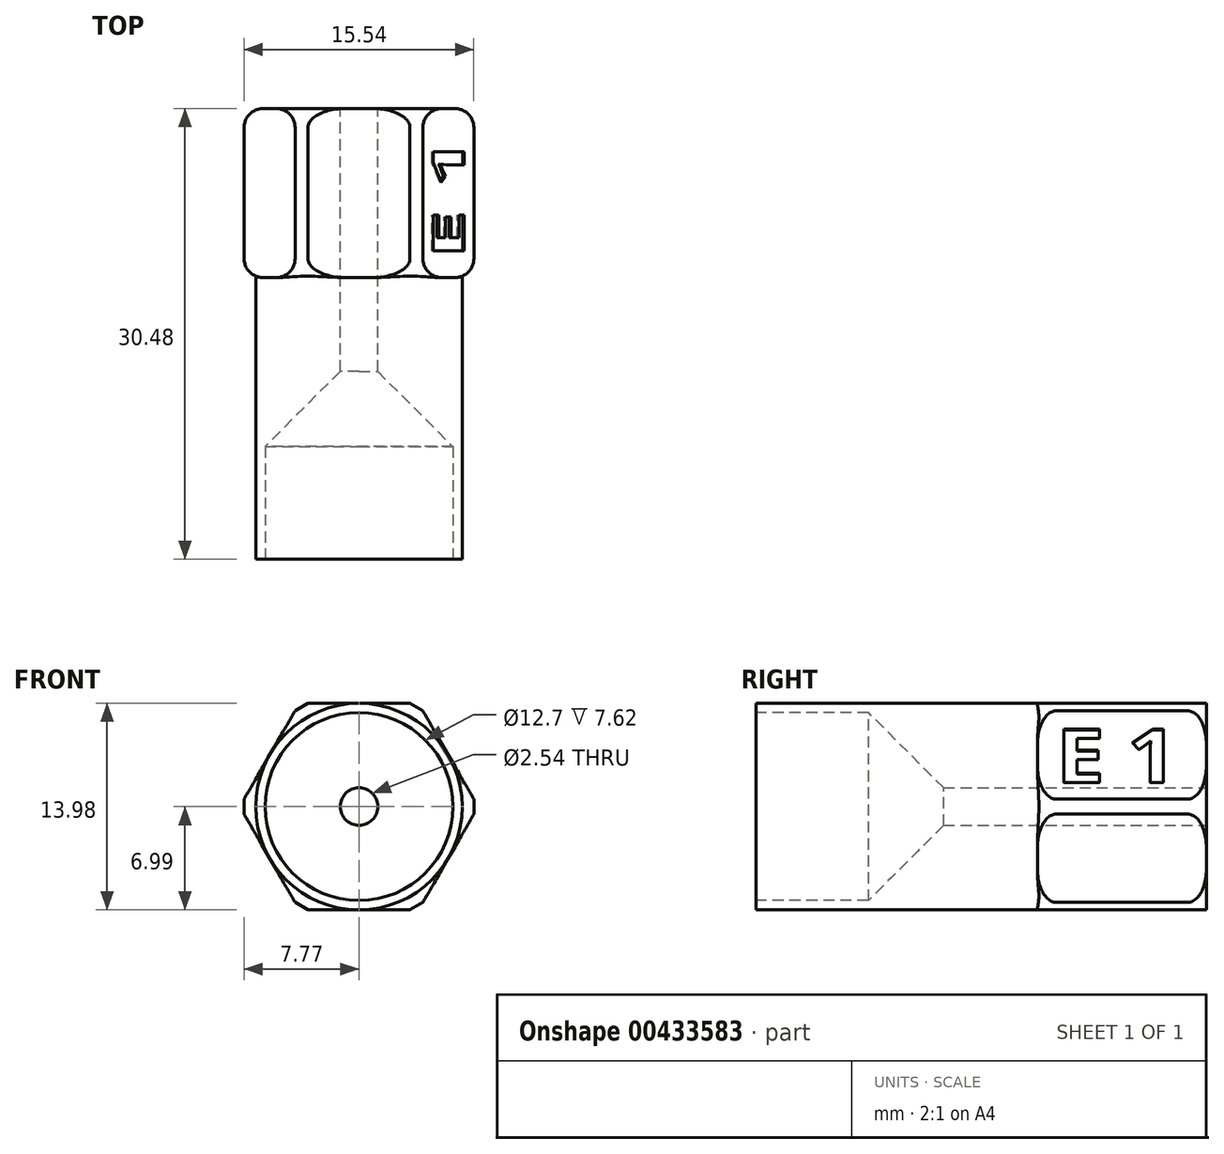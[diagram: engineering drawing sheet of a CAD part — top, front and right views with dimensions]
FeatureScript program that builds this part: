
annotation { "Feature Type Name" : "Feature", "Feature Type Description" : "" }
export const myFeature = defineFeature(function(context is Context, id is Id, definition is map)
    precondition{}
    {
        {
            var Q0;
            Q0=qCreatedBy(makeId("Front.planeOp"),FACE);
            var sketch = newSketch(context, id + "F0", { "sketchPlane" : qUnion([Q0])});
            skCircle(sketch, "E0.cCircle", {"center": v(0, 0) * mm, "radius": 6.99 * mm, "construction": true});
            skLineSegment(sketch, "E0.0", {"start": v(-4.03, 6.99) * mm, "end": v(4.03, 6.99) * mm});
            skLineSegment(sketch, "E0.1", {"start": v(4.03, 6.99) * mm, "end": v(8.07, 0) * mm});
            skLineSegment(sketch, "E0.2", {"start": v(8.07, 0) * mm, "end": v(4.03, -6.98) * mm});
            skLineSegment(sketch, "E0.3", {"start": v(4.03, -6.98) * mm, "end": v(-4.03, -6.99) * mm});
            skLineSegment(sketch, "E0.4", {"start": v(-4.03, -6.99) * mm, "end": v(-8.07, 0) * mm});
            skLineSegment(sketch, "E0.5", {"start": v(-8.07, 0) * mm, "end": v(-4.03, 6.99) * mm});
            skPoint(sketch, "E0.0.midPoint", {"position": v(0, 6.99) * mm});
            skSolve(sketch);
        }
        {
            var Q0;
            Q0=makeQuery(id+"F0.imprint","IMPRINT",FACE,{"disambiguationData":[TD([[makeQuery(id+"F0.imprint","IMPRINT",EDGE,{"derivedFrom":sQuery(id+"F0.wireOp",EDGE,"E0.0")}),-1.0]])]});
            extrude(context, id + "F1", {"entities" : qUnion([Q0]), "depth" : 11.43 * mm});
        }
        {
            var Q0;
            Q0=makeQuery(id+"F1.opExtrude","CAP_FACE",FACE,{"disambiguationData":[OSD([sQuery(id+"F0.wireOp",EDGE,"E0.0"),sQuery(id+"F0.wireOp",EDGE,"E0.1"),sQuery(id+"F0.wireOp",EDGE,"E0.2"),sQuery(id+"F0.wireOp",EDGE,"E0.3"),sQuery(id+"F0.wireOp",EDGE,"E0.4"),sQuery(id+"F0.wireOp",EDGE,"E0.5")])],"isStart":false});
            var sketch = newSketch(context, id + "F2", { "sketchPlane" : qUnion([Q0])});
            skCircle(sketch, "E1", {"center": v(0, 0) * mm, "radius": 6.99 * mm});
            skSolve(sketch);
        }
        {
            var Q0;
            {var subQ0=sQuery(id+"F2.wireOp",EDGE,"E1");var subQ4=makeQuery(id+"F2.imprint","INTERSECT",VERTEX,{"derivedFrom":[makeQuery(id+"F1.opExtrude","CAP_EDGE",EDGE,{"disambiguationData":[OSD([sQuery(id+"F0.wireOp",EDGE,"E0.0")])],"isStart":false}),subQ0]});Q0=makeQuery(id+"F2.imprint","IMPRINT",FACE,{"disambiguationData":[TD([[makeQuery(id+"F2.imprint","IMPRINT",EDGE,{"disambiguationData":[TD([[subQ4,1.0]])],"derivedFrom":subQ0}),1.0]])]});}
            extrude(context, id + "F3", {"entities" : qUnion([Q0]), "operationType" : NewBodyOperationType.ADD, "depth" : 19.05 * mm});
        }
        {
            var Q0;
            Q0=makeQuery(id+"F3.opExtrude","CAP_FACE",FACE,{"disambiguationData":[OSD([sQuery(id+"F2.wireOp",EDGE,"E1")])],"isStart":false});
            var sketch = newSketch(context, id + "F4", { "sketchPlane" : qUnion([Q0])});
            skCircle(sketch, "E2", {"center": v(0, 0) * mm, "radius": 6.35 * mm});
            skSolve(sketch);
        }
        {
            var Q0;
            Q0=makeQuery(id+"F4.imprint","IMPRINT",FACE,{"disambiguationData":[TD([[makeQuery(id+"F4.imprint","IMPRINT",EDGE,{"derivedFrom":sQuery(id+"F4.wireOp",EDGE,"E2")}),1.0]])]});
            extrude(context, id + "F5", {"entities" : qUnion([Q0]), "operationType" : NewBodyOperationType.REMOVE, "oppositeDirection" : true, "depth" : 12.7 * mm});
        }
        {
            var Q0;
            Q0=makeQuery(id+"F5.boolean.opBoolean","COPY",EDGE,{"derivedFrom":makeQuery(id+"F5.opExtrude","CAP_EDGE",EDGE,{"disambiguationData":[OSD([sQuery(id+"F4.wireOp",EDGE,"E2")])],"isStart":false})});
            chamfer(context, id + "F6", {"entities" : qUnion([Q0]), "width" : 5.08 * mm, "tangentPropagation" : true});
        }
        {
            var Q0;
            Q0=makeQuery(id+"F1.opExtrude","SWEPT_EDGE",EDGE,{"disambiguationData":[OSD([sQuery(id+"F0.wireOp",EDGE,"E0.0"),sQuery(id+"F0.wireOp",EDGE,"E0.5")])]});
            var Q1;
            Q1=makeQuery(id+"F1.opExtrude","SWEPT_EDGE",EDGE,{"disambiguationData":[OSD([sQuery(id+"F0.wireOp",EDGE,"E0.0"),sQuery(id+"F0.wireOp",EDGE,"E0.1")])]});
            var Q2;
            Q2=makeQuery(id+"F1.opExtrude","SWEPT_EDGE",EDGE,{"disambiguationData":[OSD([sQuery(id+"F0.wireOp",EDGE,"E0.1"),sQuery(id+"F0.wireOp",EDGE,"E0.2")])]});
            var Q3;
            Q3=makeQuery(id+"F1.opExtrude","SWEPT_EDGE",EDGE,{"disambiguationData":[OSD([sQuery(id+"F0.wireOp",EDGE,"E0.2"),sQuery(id+"F0.wireOp",EDGE,"E0.3")])]});
            var Q4;
            Q4=makeQuery(id+"F1.opExtrude","SWEPT_EDGE",EDGE,{"disambiguationData":[OSD([sQuery(id+"F0.wireOp",EDGE,"E0.3"),sQuery(id+"F0.wireOp",EDGE,"E0.4")])]});
            var Q5;
            Q5=makeQuery(id+"F1.opExtrude","SWEPT_EDGE",EDGE,{"disambiguationData":[OSD([sQuery(id+"F0.wireOp",EDGE,"E0.4"),sQuery(id+"F0.wireOp",EDGE,"E0.5")])]});
            chamfer(context, id + "F7", {"entities" : qUnion([Q0, Q1, Q2, Q3, Q4, Q5]), "width" : 1.02 * mm, "tangentPropagation" : true});
        }
        {
            var Q0;
            {var subQ0=sQuery(id+"F0.wireOp",EDGE,"E0.2");var subQ1=sQuery(id+"F0.wireOp",EDGE,"E0.1");var subQ2=makeQuery(id+"F1.opExtrude","CAP_FACE",FACE,{"disambiguationData":[OSD([sQuery(id+"F0.wireOp",EDGE,"E0.0"),subQ1,subQ0,sQuery(id+"F0.wireOp",EDGE,"E0.3"),sQuery(id+"F0.wireOp",EDGE,"E0.4"),sQuery(id+"F0.wireOp",EDGE,"E0.5")])],"isStart":false});Q0=makeQuery(id+"F7.opChamfer","BLEND_EDGE",EDGE,{"blendedFrom":[makeQuery(id+"F1.opExtrude","SWEPT_EDGE",EDGE,{"disambiguationData":[OSD([subQ1,subQ0])]}),makeQuery(id+"F3.boolean.opBoolean","SPLIT",FACE,{"disambiguationData":[TD([subQ2,makeQuery(id+"F1.opExtrude","SWEPT_FACE",FACE,{"disambiguationData":[OSD([subQ1])]}),makeQuery(id+"F1.opExtrude","SWEPT_FACE",FACE,{"disambiguationData":[OSD([subQ0])]}),makeQuery(id+"F3.opExtrude","SWEPT_FACE",FACE,{"disambiguationData":[OSD([sQuery(id+"F2.wireOp",EDGE,"E1")])]})])],"derivedFrom":subQ2})],"blendedInto":[makeQuery(id+"F3.boolean.opBoolean","SPLIT",FACE,{"disambiguationData":[TD([subQ2,makeQuery(id+"F1.opExtrude","SWEPT_FACE",FACE,{"disambiguationData":[OSD([subQ1])]}),makeQuery(id+"F1.opExtrude","SWEPT_FACE",FACE,{"disambiguationData":[OSD([subQ0])]}),makeQuery(id+"F3.opExtrude","SWEPT_FACE",FACE,{"disambiguationData":[OSD([sQuery(id+"F2.wireOp",EDGE,"E1")])]})])],"derivedFrom":subQ2})]});}
            var Q1;
            {var subQ0=sQuery(id+"F0.wireOp",EDGE,"E0.3");var subQ1=sQuery(id+"F0.wireOp",EDGE,"E0.2");var subQ2=makeQuery(id+"F1.opExtrude","CAP_FACE",FACE,{"disambiguationData":[OSD([sQuery(id+"F0.wireOp",EDGE,"E0.0"),sQuery(id+"F0.wireOp",EDGE,"E0.1"),subQ1,subQ0,sQuery(id+"F0.wireOp",EDGE,"E0.4"),sQuery(id+"F0.wireOp",EDGE,"E0.5")])],"isStart":false});Q1=makeQuery(id+"F7.opChamfer","BLEND_EDGE",EDGE,{"blendedFrom":[makeQuery(id+"F1.opExtrude","SWEPT_EDGE",EDGE,{"disambiguationData":[OSD([subQ1,subQ0])]}),makeQuery(id+"F3.boolean.opBoolean","SPLIT",FACE,{"disambiguationData":[TD([subQ2,makeQuery(id+"F1.opExtrude","SWEPT_FACE",FACE,{"disambiguationData":[OSD([subQ1])]}),makeQuery(id+"F1.opExtrude","SWEPT_FACE",FACE,{"disambiguationData":[OSD([subQ0])]}),makeQuery(id+"F3.opExtrude","SWEPT_FACE",FACE,{"disambiguationData":[OSD([sQuery(id+"F2.wireOp",EDGE,"E1")])]})])],"derivedFrom":subQ2})],"blendedInto":[makeQuery(id+"F3.boolean.opBoolean","SPLIT",FACE,{"disambiguationData":[TD([subQ2,makeQuery(id+"F1.opExtrude","SWEPT_FACE",FACE,{"disambiguationData":[OSD([subQ1])]}),makeQuery(id+"F1.opExtrude","SWEPT_FACE",FACE,{"disambiguationData":[OSD([subQ0])]}),makeQuery(id+"F3.opExtrude","SWEPT_FACE",FACE,{"disambiguationData":[OSD([sQuery(id+"F2.wireOp",EDGE,"E1")])]})])],"derivedFrom":subQ2})]});}
            var Q2;
            {var subQ0=sQuery(id+"F0.wireOp",EDGE,"E0.4");var subQ1=sQuery(id+"F0.wireOp",EDGE,"E0.3");var subQ2=makeQuery(id+"F1.opExtrude","CAP_FACE",FACE,{"disambiguationData":[OSD([sQuery(id+"F0.wireOp",EDGE,"E0.0"),sQuery(id+"F0.wireOp",EDGE,"E0.1"),sQuery(id+"F0.wireOp",EDGE,"E0.2"),subQ1,subQ0,sQuery(id+"F0.wireOp",EDGE,"E0.5")])],"isStart":false});Q2=makeQuery(id+"F7.opChamfer","BLEND_EDGE",EDGE,{"blendedFrom":[makeQuery(id+"F1.opExtrude","SWEPT_EDGE",EDGE,{"disambiguationData":[OSD([subQ1,subQ0])]}),makeQuery(id+"F3.boolean.opBoolean","SPLIT",FACE,{"disambiguationData":[TD([subQ2,makeQuery(id+"F1.opExtrude","SWEPT_FACE",FACE,{"disambiguationData":[OSD([subQ1])]}),makeQuery(id+"F1.opExtrude","SWEPT_FACE",FACE,{"disambiguationData":[OSD([subQ0])]}),makeQuery(id+"F3.opExtrude","SWEPT_FACE",FACE,{"disambiguationData":[OSD([sQuery(id+"F2.wireOp",EDGE,"E1")])]})])],"derivedFrom":subQ2})],"blendedInto":[makeQuery(id+"F3.boolean.opBoolean","SPLIT",FACE,{"disambiguationData":[TD([subQ2,makeQuery(id+"F1.opExtrude","SWEPT_FACE",FACE,{"disambiguationData":[OSD([subQ1])]}),makeQuery(id+"F1.opExtrude","SWEPT_FACE",FACE,{"disambiguationData":[OSD([subQ0])]}),makeQuery(id+"F3.opExtrude","SWEPT_FACE",FACE,{"disambiguationData":[OSD([sQuery(id+"F2.wireOp",EDGE,"E1")])]})])],"derivedFrom":subQ2})]});}
            var Q3;
            {var subQ0=sQuery(id+"F0.wireOp",EDGE,"E0.5");var subQ1=sQuery(id+"F0.wireOp",EDGE,"E0.4");var subQ2=makeQuery(id+"F1.opExtrude","CAP_FACE",FACE,{"disambiguationData":[OSD([sQuery(id+"F0.wireOp",EDGE,"E0.0"),sQuery(id+"F0.wireOp",EDGE,"E0.1"),sQuery(id+"F0.wireOp",EDGE,"E0.2"),sQuery(id+"F0.wireOp",EDGE,"E0.3"),subQ1,subQ0])],"isStart":false});Q3=makeQuery(id+"F7.opChamfer","BLEND_EDGE",EDGE,{"blendedFrom":[makeQuery(id+"F1.opExtrude","SWEPT_EDGE",EDGE,{"disambiguationData":[OSD([subQ1,subQ0])]}),makeQuery(id+"F3.boolean.opBoolean","SPLIT",FACE,{"disambiguationData":[TD([subQ2,makeQuery(id+"F1.opExtrude","SWEPT_FACE",FACE,{"disambiguationData":[OSD([subQ1])]}),makeQuery(id+"F1.opExtrude","SWEPT_FACE",FACE,{"disambiguationData":[OSD([subQ0])]}),makeQuery(id+"F3.opExtrude","SWEPT_FACE",FACE,{"disambiguationData":[OSD([sQuery(id+"F2.wireOp",EDGE,"E1")])]})])],"derivedFrom":subQ2})],"blendedInto":[makeQuery(id+"F3.boolean.opBoolean","SPLIT",FACE,{"disambiguationData":[TD([subQ2,makeQuery(id+"F1.opExtrude","SWEPT_FACE",FACE,{"disambiguationData":[OSD([subQ1])]}),makeQuery(id+"F1.opExtrude","SWEPT_FACE",FACE,{"disambiguationData":[OSD([subQ0])]}),makeQuery(id+"F3.opExtrude","SWEPT_FACE",FACE,{"disambiguationData":[OSD([sQuery(id+"F2.wireOp",EDGE,"E1")])]})])],"derivedFrom":subQ2})]});}
            var Q4;
            {var subQ0=sQuery(id+"F0.wireOp",EDGE,"E0.0");var subQ1=sQuery(id+"F0.wireOp",EDGE,"E0.5");var subQ2=makeQuery(id+"F1.opExtrude","CAP_FACE",FACE,{"disambiguationData":[OSD([subQ0,sQuery(id+"F0.wireOp",EDGE,"E0.1"),sQuery(id+"F0.wireOp",EDGE,"E0.2"),sQuery(id+"F0.wireOp",EDGE,"E0.3"),sQuery(id+"F0.wireOp",EDGE,"E0.4"),subQ1])],"isStart":false});Q4=makeQuery(id+"F7.opChamfer","BLEND_EDGE",EDGE,{"blendedFrom":[makeQuery(id+"F1.opExtrude","SWEPT_EDGE",EDGE,{"disambiguationData":[OSD([subQ0,subQ1])]}),makeQuery(id+"F3.boolean.opBoolean","SPLIT",FACE,{"disambiguationData":[TD([makeQuery(id+"F1.opExtrude","SWEPT_FACE",FACE,{"disambiguationData":[OSD([subQ0])]}),subQ2,makeQuery(id+"F1.opExtrude","SWEPT_FACE",FACE,{"disambiguationData":[OSD([subQ1])]}),makeQuery(id+"F3.opExtrude","SWEPT_FACE",FACE,{"disambiguationData":[OSD([sQuery(id+"F2.wireOp",EDGE,"E1")])]})])],"derivedFrom":subQ2})],"blendedInto":[makeQuery(id+"F3.boolean.opBoolean","SPLIT",FACE,{"disambiguationData":[TD([makeQuery(id+"F1.opExtrude","SWEPT_FACE",FACE,{"disambiguationData":[OSD([subQ0])]}),subQ2,makeQuery(id+"F1.opExtrude","SWEPT_FACE",FACE,{"disambiguationData":[OSD([subQ1])]}),makeQuery(id+"F3.opExtrude","SWEPT_FACE",FACE,{"disambiguationData":[OSD([sQuery(id+"F2.wireOp",EDGE,"E1")])]})])],"derivedFrom":subQ2})]});}
            var Q5;
            {var subQ0=sQuery(id+"F0.wireOp",EDGE,"E0.0");var subQ1=sQuery(id+"F0.wireOp",EDGE,"E0.1");var subQ2=makeQuery(id+"F1.opExtrude","CAP_FACE",FACE,{"disambiguationData":[OSD([subQ0,subQ1,sQuery(id+"F0.wireOp",EDGE,"E0.2"),sQuery(id+"F0.wireOp",EDGE,"E0.3"),sQuery(id+"F0.wireOp",EDGE,"E0.4"),sQuery(id+"F0.wireOp",EDGE,"E0.5")])],"isStart":false});Q5=makeQuery(id+"F7.opChamfer","BLEND_EDGE",EDGE,{"blendedFrom":[makeQuery(id+"F1.opExtrude","SWEPT_EDGE",EDGE,{"disambiguationData":[OSD([subQ0,subQ1])]}),makeQuery(id+"F3.boolean.opBoolean","SPLIT",FACE,{"disambiguationData":[TD([makeQuery(id+"F1.opExtrude","SWEPT_FACE",FACE,{"disambiguationData":[OSD([subQ0])]}),subQ2,makeQuery(id+"F1.opExtrude","SWEPT_FACE",FACE,{"disambiguationData":[OSD([subQ1])]}),makeQuery(id+"F3.opExtrude","SWEPT_FACE",FACE,{"disambiguationData":[OSD([sQuery(id+"F2.wireOp",EDGE,"E1")])]})])],"derivedFrom":subQ2})],"blendedInto":[makeQuery(id+"F3.boolean.opBoolean","SPLIT",FACE,{"disambiguationData":[TD([makeQuery(id+"F1.opExtrude","SWEPT_FACE",FACE,{"disambiguationData":[OSD([subQ0])]}),subQ2,makeQuery(id+"F1.opExtrude","SWEPT_FACE",FACE,{"disambiguationData":[OSD([subQ1])]}),makeQuery(id+"F3.opExtrude","SWEPT_FACE",FACE,{"disambiguationData":[OSD([sQuery(id+"F2.wireOp",EDGE,"E1")])]})])],"derivedFrom":subQ2})]});}
            var Q6;
            {var subQ0=sQuery(id+"F0.wireOp",EDGE,"E0.2");var subQ1=sQuery(id+"F0.wireOp",EDGE,"E0.1");Q6=makeQuery(id+"F7.opChamfer","BLEND_EDGE",EDGE,{"blendedFrom":[makeQuery(id+"F1.opExtrude","SWEPT_EDGE",EDGE,{"disambiguationData":[OSD([subQ1,subQ0])]}),makeQuery(id+"F1.opExtrude","CAP_FACE",FACE,{"disambiguationData":[OSD([sQuery(id+"F0.wireOp",EDGE,"E0.0"),subQ1,subQ0,sQuery(id+"F0.wireOp",EDGE,"E0.3"),sQuery(id+"F0.wireOp",EDGE,"E0.4"),sQuery(id+"F0.wireOp",EDGE,"E0.5")])],"isStart":true})],"blendedInto":[makeQuery(id+"F1.opExtrude","CAP_FACE",FACE,{"disambiguationData":[OSD([sQuery(id+"F0.wireOp",EDGE,"E0.0"),subQ1,subQ0,sQuery(id+"F0.wireOp",EDGE,"E0.3"),sQuery(id+"F0.wireOp",EDGE,"E0.4"),sQuery(id+"F0.wireOp",EDGE,"E0.5")])],"isStart":true})]});}
            var Q7;
            {var subQ0=sQuery(id+"F0.wireOp",EDGE,"E0.3");var subQ1=sQuery(id+"F0.wireOp",EDGE,"E0.2");Q7=makeQuery(id+"F7.opChamfer","BLEND_EDGE",EDGE,{"blendedFrom":[makeQuery(id+"F1.opExtrude","SWEPT_EDGE",EDGE,{"disambiguationData":[OSD([subQ1,subQ0])]}),makeQuery(id+"F1.opExtrude","CAP_FACE",FACE,{"disambiguationData":[OSD([sQuery(id+"F0.wireOp",EDGE,"E0.0"),sQuery(id+"F0.wireOp",EDGE,"E0.1"),subQ1,subQ0,sQuery(id+"F0.wireOp",EDGE,"E0.4"),sQuery(id+"F0.wireOp",EDGE,"E0.5")])],"isStart":true})],"blendedInto":[makeQuery(id+"F1.opExtrude","CAP_FACE",FACE,{"disambiguationData":[OSD([sQuery(id+"F0.wireOp",EDGE,"E0.0"),sQuery(id+"F0.wireOp",EDGE,"E0.1"),subQ1,subQ0,sQuery(id+"F0.wireOp",EDGE,"E0.4"),sQuery(id+"F0.wireOp",EDGE,"E0.5")])],"isStart":true})]});}
            var Q8;
            {var subQ0=sQuery(id+"F0.wireOp",EDGE,"E0.4");var subQ1=sQuery(id+"F0.wireOp",EDGE,"E0.3");Q8=makeQuery(id+"F7.opChamfer","BLEND_EDGE",EDGE,{"blendedFrom":[makeQuery(id+"F1.opExtrude","SWEPT_EDGE",EDGE,{"disambiguationData":[OSD([subQ1,subQ0])]}),makeQuery(id+"F1.opExtrude","CAP_FACE",FACE,{"disambiguationData":[OSD([sQuery(id+"F0.wireOp",EDGE,"E0.0"),sQuery(id+"F0.wireOp",EDGE,"E0.1"),sQuery(id+"F0.wireOp",EDGE,"E0.2"),subQ1,subQ0,sQuery(id+"F0.wireOp",EDGE,"E0.5")])],"isStart":true})],"blendedInto":[makeQuery(id+"F1.opExtrude","CAP_FACE",FACE,{"disambiguationData":[OSD([sQuery(id+"F0.wireOp",EDGE,"E0.0"),sQuery(id+"F0.wireOp",EDGE,"E0.1"),sQuery(id+"F0.wireOp",EDGE,"E0.2"),subQ1,subQ0,sQuery(id+"F0.wireOp",EDGE,"E0.5")])],"isStart":true})]});}
            var Q9;
            {var subQ0=sQuery(id+"F0.wireOp",EDGE,"E0.5");var subQ1=sQuery(id+"F0.wireOp",EDGE,"E0.4");Q9=makeQuery(id+"F7.opChamfer","BLEND_EDGE",EDGE,{"blendedFrom":[makeQuery(id+"F1.opExtrude","SWEPT_EDGE",EDGE,{"disambiguationData":[OSD([subQ1,subQ0])]}),makeQuery(id+"F1.opExtrude","CAP_FACE",FACE,{"disambiguationData":[OSD([sQuery(id+"F0.wireOp",EDGE,"E0.0"),sQuery(id+"F0.wireOp",EDGE,"E0.1"),sQuery(id+"F0.wireOp",EDGE,"E0.2"),sQuery(id+"F0.wireOp",EDGE,"E0.3"),subQ1,subQ0])],"isStart":true})],"blendedInto":[makeQuery(id+"F1.opExtrude","CAP_FACE",FACE,{"disambiguationData":[OSD([sQuery(id+"F0.wireOp",EDGE,"E0.0"),sQuery(id+"F0.wireOp",EDGE,"E0.1"),sQuery(id+"F0.wireOp",EDGE,"E0.2"),sQuery(id+"F0.wireOp",EDGE,"E0.3"),subQ1,subQ0])],"isStart":true})]});}
            var Q10;
            {var subQ0=sQuery(id+"F0.wireOp",EDGE,"E0.5");var subQ1=sQuery(id+"F0.wireOp",EDGE,"E0.0");Q10=makeQuery(id+"F7.opChamfer","BLEND_EDGE",EDGE,{"blendedFrom":[makeQuery(id+"F1.opExtrude","SWEPT_EDGE",EDGE,{"disambiguationData":[OSD([subQ1,subQ0])]}),makeQuery(id+"F1.opExtrude","CAP_FACE",FACE,{"disambiguationData":[OSD([subQ1,sQuery(id+"F0.wireOp",EDGE,"E0.1"),sQuery(id+"F0.wireOp",EDGE,"E0.2"),sQuery(id+"F0.wireOp",EDGE,"E0.3"),sQuery(id+"F0.wireOp",EDGE,"E0.4"),subQ0])],"isStart":true})],"blendedInto":[makeQuery(id+"F1.opExtrude","CAP_FACE",FACE,{"disambiguationData":[OSD([subQ1,sQuery(id+"F0.wireOp",EDGE,"E0.1"),sQuery(id+"F0.wireOp",EDGE,"E0.2"),sQuery(id+"F0.wireOp",EDGE,"E0.3"),sQuery(id+"F0.wireOp",EDGE,"E0.4"),subQ0])],"isStart":true})]});}
            var Q11;
            {var subQ0=sQuery(id+"F0.wireOp",EDGE,"E0.1");var subQ1=sQuery(id+"F0.wireOp",EDGE,"E0.0");Q11=makeQuery(id+"F7.opChamfer","BLEND_EDGE",EDGE,{"blendedFrom":[makeQuery(id+"F1.opExtrude","SWEPT_EDGE",EDGE,{"disambiguationData":[OSD([subQ1,subQ0])]}),makeQuery(id+"F1.opExtrude","CAP_FACE",FACE,{"disambiguationData":[OSD([subQ1,subQ0,sQuery(id+"F0.wireOp",EDGE,"E0.2"),sQuery(id+"F0.wireOp",EDGE,"E0.3"),sQuery(id+"F0.wireOp",EDGE,"E0.4"),sQuery(id+"F0.wireOp",EDGE,"E0.5")])],"isStart":true})],"blendedInto":[makeQuery(id+"F1.opExtrude","CAP_FACE",FACE,{"disambiguationData":[OSD([subQ1,subQ0,sQuery(id+"F0.wireOp",EDGE,"E0.2"),sQuery(id+"F0.wireOp",EDGE,"E0.3"),sQuery(id+"F0.wireOp",EDGE,"E0.4"),sQuery(id+"F0.wireOp",EDGE,"E0.5")])],"isStart":true})]});}
            fillet(context, id + "F8", {"entities" : qUnion([Q0, Q1, Q2, Q3, Q4, Q5, Q6, Q7, Q8, Q9, Q10, Q11]), "radius" : 1.27 * mm, "tangentPropagation" : true, "allowEdgeOverflow" : false});
        }
        {
            var Q0;
            Q0=makeQuery(id+"F1.opExtrude","SWEPT_FACE",FACE,{"disambiguationData":[OSD([sQuery(id+"F0.wireOp",EDGE,"E0.1")])]});
            var sketch = newSketch(context, id + "F9", { "sketchPlane" : qUnion([Q0])});
            skText(sketch, "E3", { "text": "E 1", "fontName": "OpenSans-Bold.ttf"});
            skPoint(sketch, "E3.firstSnap0", {"position": v(-2.54, -0.48) * mm});
            const initialGuessF9  = {"E3": [-0.01016, -0.00216, 1, 0, 0.00423]};
            skSetInitialGuess(sketch, initialGuessF9);
            skSolve(sketch);
        }
        {
            var Q0;
            Q0=qSketchRegion(id+"F9",true);
            extrude(context, id + "F10", {"entities" : qUnion([Q0]), "operationType" : NewBodyOperationType.REMOVE, "oppositeDirection" : true, "depth" : 0.13 * mm});
        }
        {
            var Q0;
            Q0=makeQuery(id+"F1.opExtrude","CAP_FACE",FACE,{"disambiguationData":[OSD([sQuery(id+"F0.wireOp",EDGE,"E0.0"),sQuery(id+"F0.wireOp",EDGE,"E0.1"),sQuery(id+"F0.wireOp",EDGE,"E0.2"),sQuery(id+"F0.wireOp",EDGE,"E0.3"),sQuery(id+"F0.wireOp",EDGE,"E0.4"),sQuery(id+"F0.wireOp",EDGE,"E0.5")])],"isStart":true});
            var sketch = newSketch(context, id + "F11", { "sketchPlane" : qUnion([Q0])});
            skCircle(sketch, "E4", {"center": v(0, 0) * mm, "radius": 1.27 * mm});
            skSolve(sketch);
        }
        {
            var Q0;
            Q0=makeQuery(id+"F11.imprint","IMPRINT",FACE,{"disambiguationData":[TD([[makeQuery(id+"F11.imprint","IMPRINT",EDGE,{"derivedFrom":sQuery(id+"F11.wireOp",EDGE,"E4")}),1.0]])]});
            extrude(context, id + "F12", {"entities" : qUnion([Q0]), "operationType" : NewBodyOperationType.REMOVE, "endBound" : BoundingType.THROUGH_ALL, "oppositeDirection" : true, "depth" : 25.4 * mm});
        }
    });
